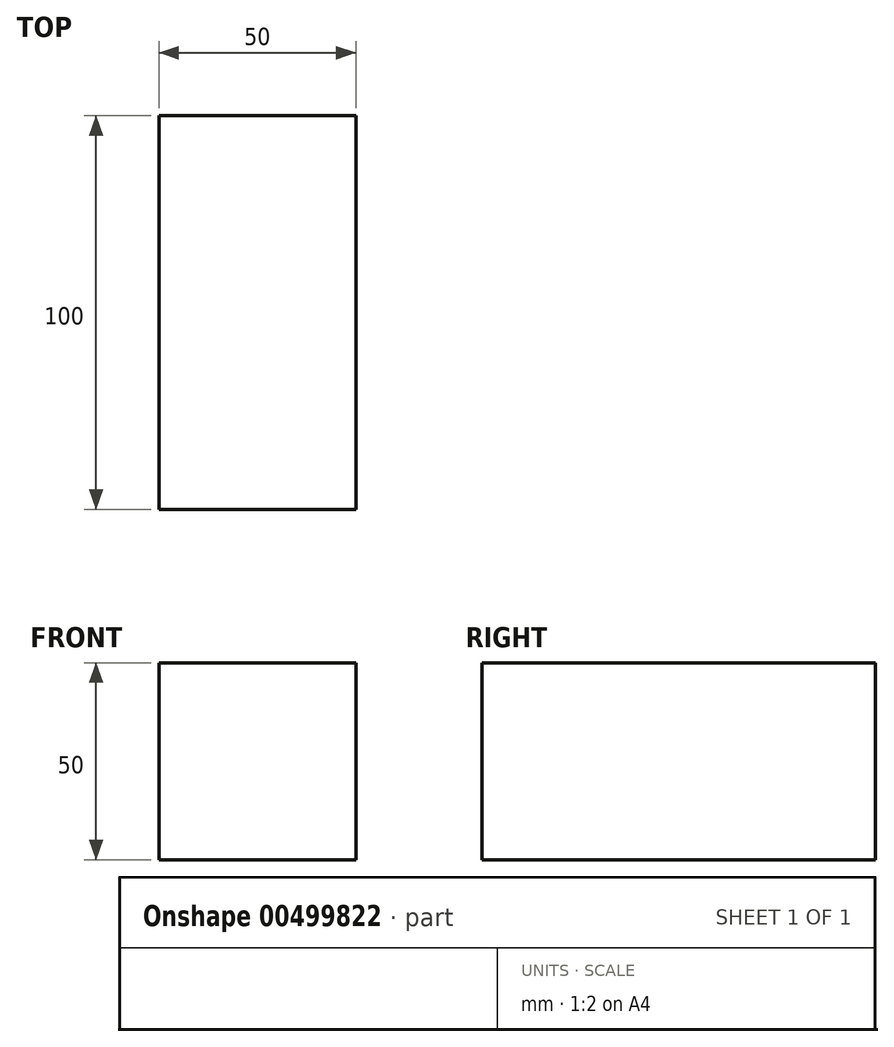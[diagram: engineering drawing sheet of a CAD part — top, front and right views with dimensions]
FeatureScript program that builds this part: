
annotation { "Feature Type Name" : "Feature", "Feature Type Description" : "" }
export const myFeature = defineFeature(function(context is Context, id is Id, definition is map)
    precondition{}
    {
        {
            var Q0;
            Q0=qCreatedBy(makeId("Front.planeOp"),FACE);
            var sketch = newSketch(context, id + "F0", { "sketchPlane" : qUnion([Q0])});
            skLineSegment(sketch, "E0.bottom", {"start": v(25, 25) * mm, "end": v(-25, 25) * mm});
            skLineSegment(sketch, "E0.top", {"start": v(25, -25) * mm, "end": v(-25, -25) * mm});
            skLineSegment(sketch, "E0.left", {"start": v(25, 25) * mm, "end": v(25, -25) * mm});
            skLineSegment(sketch, "E0.right", {"start": v(-25, 25) * mm, "end": v(-25, -25) * mm});
            skPoint(sketch, "E0.middle", {"position": v(0, 0) * mm});
            skSolve(sketch);
        }
        {
            var Q0;
            Q0 = qSketchRegion(id + "F0", true);
            extrude(context, id + "F1", {"entities" : qUnion([Q0]), "depth" : 100 * mm, "symmetric" : true});
        }
    });
